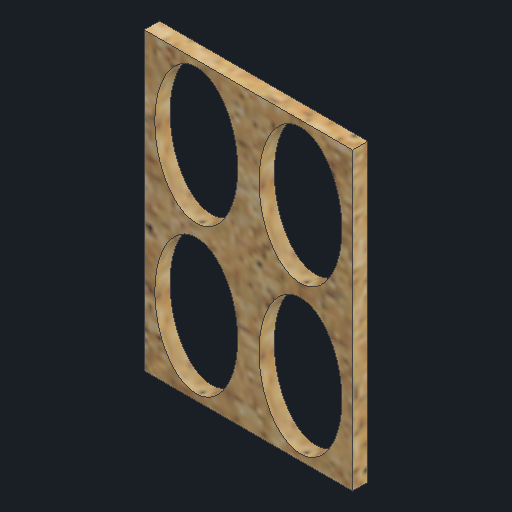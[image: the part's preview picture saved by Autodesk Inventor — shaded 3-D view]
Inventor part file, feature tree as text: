
AUTODESK INVENTOR PART (.ipt)
format: ipt  version: 2022 (Build 260153070, 153G)  size: 229,888 bytes
history: native  units: mm
features: extrude x1, sketch x1
ambient origin geometry x8: Origin, YZ Plane, XZ Plane, XY Plane, X Axis, Y Axis, Z Axis, Center Point
bodies: Body1 (feature_tree)
feature tree (2):
  extrude  "Выдавливание2"  Depth=218.0mm
  sketch  "Эскиз1"
